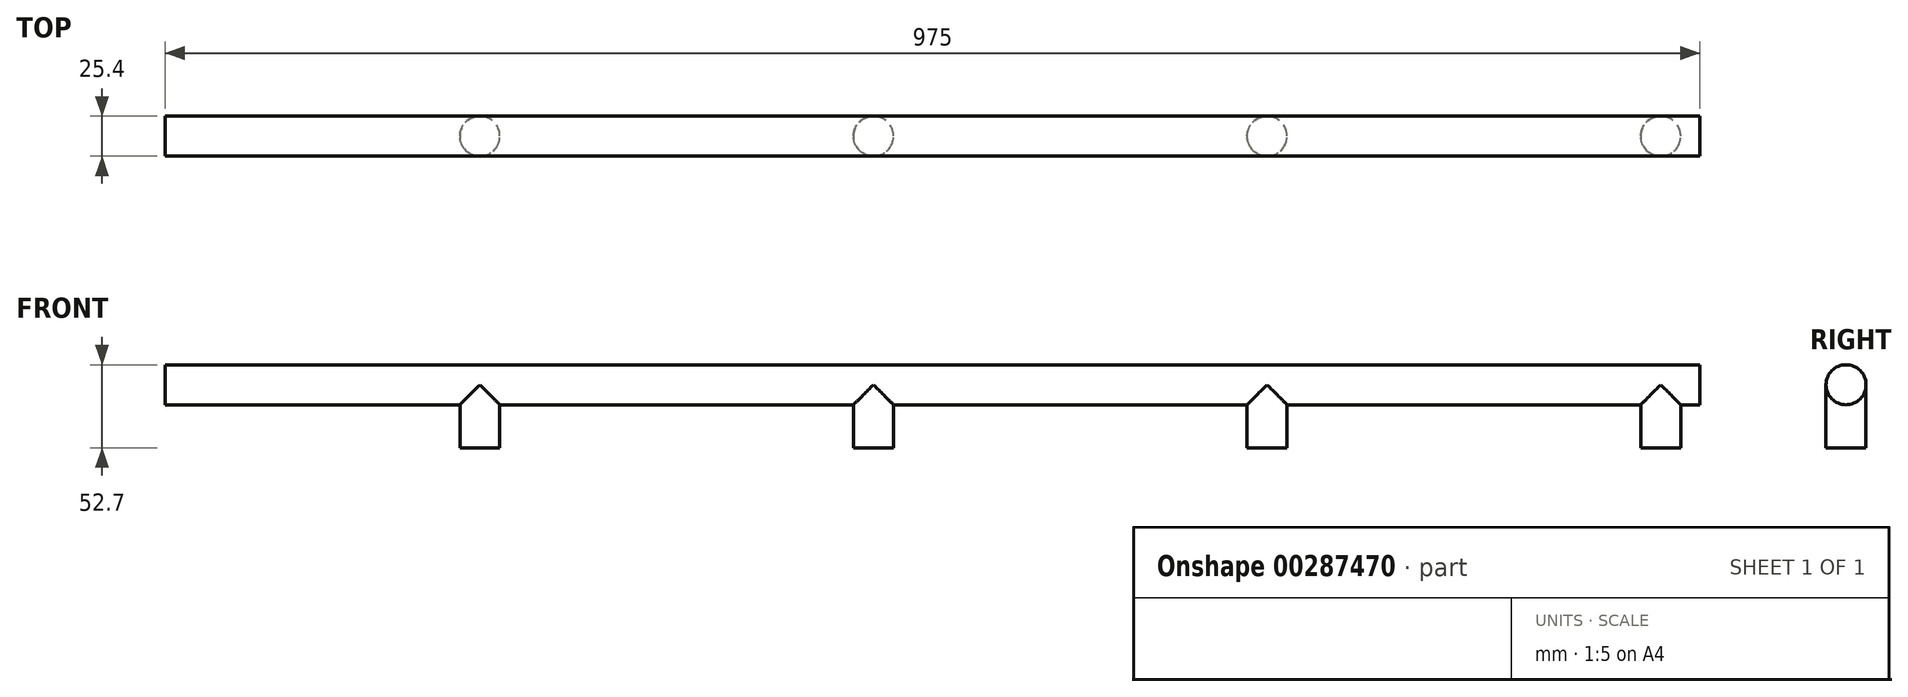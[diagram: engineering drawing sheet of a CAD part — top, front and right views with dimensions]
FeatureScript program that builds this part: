
annotation { "Feature Type Name" : "Feature", "Feature Type Description" : "" }
export const myFeature = defineFeature(function(context is Context, id is Id, definition is map)
    precondition{}
    {
        {
            var Q0;
            Q0=qCreatedBy(makeId("Right.planeOp"),FACE);
            var sketch = newSketch(context, id + "F0", { "sketchPlane" : qUnion([Q0])});
            skCircle(sketch, "E0", {"center": v(0, 0) * mm, "radius": 12.7 * mm});
            skSolve(sketch);
        }
        {
            var Q0;
            Q0=qSketchRegion(id+"F0",true);
            extrude(context, id + "F1", {"entities" : qUnion([Q0]), "oppositeDirection" : true, "depth" : 1200 * mm});
        }
        {
            var Q0;
            Q0=qCreatedBy(makeId("Top.planeOp"),FACE);
            var sketch = newSketch(context, id + "F2", { "sketchPlane" : qUnion([Q0])});
            skCircle(sketch, "E1", {"center": v(-250, 0) * mm, "radius": 12.7 * mm});
            skCircle(sketch, "E2", {"center": v(-500, 0) * mm, "radius": 12.7 * mm});
            skCircle(sketch, "E3", {"center": v(-750, 0) * mm, "radius": 12.7 * mm});
            skCircle(sketch, "E4", {"center": v(-1000, 0) * mm, "radius": 12.7 * mm});
            skSolve(sketch);
        }
        {
            var Q0;
            Q0=qSketchRegion(id+"F2",true);
            extrude(context, id + "F3", {"entities" : qUnion([Q0]), "operationType" : NewBodyOperationType.ADD, "oppositeDirection" : true, "depth" : 40 * mm});
        }
        {
            var Q0;
            Q0=makeQuery(id+"F1.opExtrude","CAP_FACE",FACE,{"disambiguationData":[OSD([sQuery(id+"F0.wireOp",EDGE,"E0")])],"isStart":true});
            extrude(context, id + "F4", {"entities" : qUnion([Q0]), "operationType" : NewBodyOperationType.REMOVE, "oppositeDirection" : true, "depth" : 225 * mm});
        }
    });
